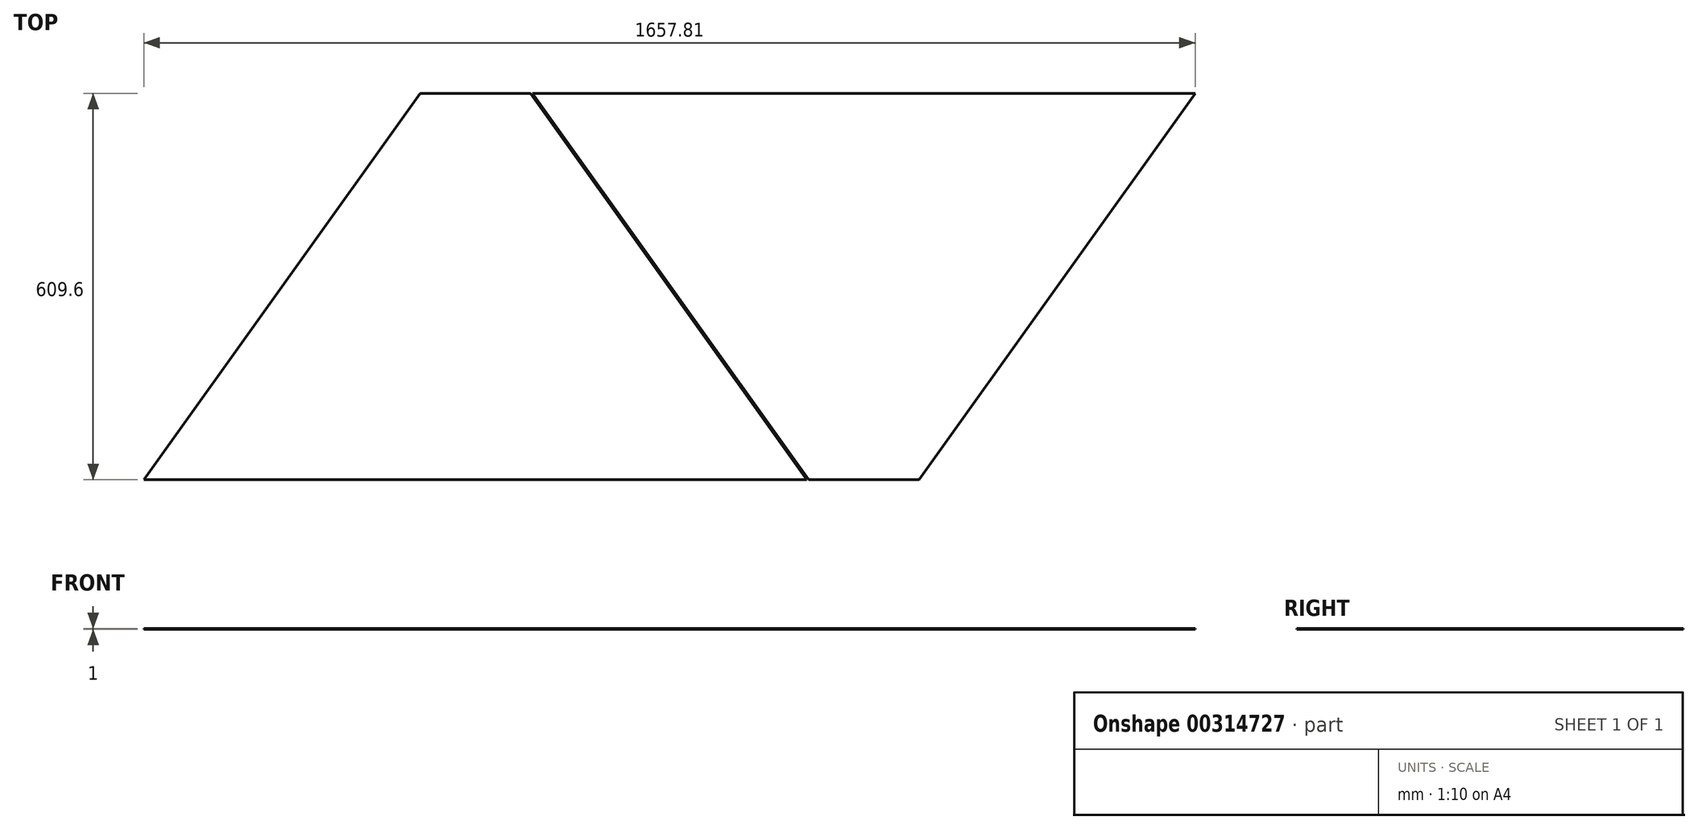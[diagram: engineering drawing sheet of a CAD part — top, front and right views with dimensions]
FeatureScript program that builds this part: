
annotation { "Feature Type Name" : "Feature", "Feature Type Description" : "" }
export const myFeature = defineFeature(function(context is Context, id is Id, definition is map)
    precondition{}
    {
        {
            var Q0;
            Q0=qCreatedBy(makeId("Top.planeOp"),FACE);
            var sketch = newSketch(context, id + "F0", { "sketchPlane" : qUnion([Q0])});
            skLineSegment(sketch, "E0", {"start": v(0, 0) * mm, "end": v(0, 609.6) * mm, "construction": true});
            skLineSegment(sketch, "E1", {"start": v(0, 0) * mm, "end": v(-522.6, 0) * mm});
            skLineSegment(sketch, "E2", {"start": v(0, 609.6) * mm, "end": v(-87, 609.6) * mm});
            skLineSegment(sketch, "E3", {"start": v(-87, 609.6) * mm, "end": v(-522.6, 0) * mm});
            skLineSegment(sketch, "E4.MirrorCS", {"start": v(0, 609.6) * mm, "end": v(87, 609.6) * mm});
            skLineSegment(sketch, "E5.MirrorCS", {"start": v(87, 609.6) * mm, "end": v(522.6, 0) * mm});
            skLineSegment(sketch, "E6.MirrorCS", {"start": v(0, 0) * mm, "end": v(522.6, 0) * mm});
            skLineSegment(sketch, "E7", {"start": v(525.6, 0) * mm, "end": v(612.6, 0) * mm});
            skLineSegment(sketch, "E8", {"start": v(525.6, 0) * mm, "end": v(90, 609.6) * mm});
            skLineSegment(sketch, "E9", {"start": v(612.6, 0) * mm, "end": v(699.6, 0) * mm});
            skLineSegment(sketch, "E10", {"start": v(90, 609.6) * mm, "end": v(612.6, 609.6) * mm});
            skLineSegment(sketch, "E11", {"start": v(612.6, 609.6) * mm, "end": v(1135.2, 609.6) * mm});
            skLineSegment(sketch, "E12", {"start": v(699.6, 0) * mm, "end": v(1135.2, 609.6) * mm});
            skSolve(sketch);
        }
        {
            var Q0;
            Q0=makeQuery(id+"F0.imprint","IMPRINT",FACE,{"disambiguationData":[TD([[makeQuery(id+"F0.imprint","IMPRINT",EDGE,{"derivedFrom":sQuery(id+"F0.wireOp",EDGE,"E1")}),-1.0]])]});
            extrude(context, id + "F1", {"entities" : qUnion([Q0]), "depth" : 1 * mm});
        }
        {
            var Q0;
            Q0=makeQuery(id+"F0.imprint","IMPRINT",FACE,{"disambiguationData":[TD([[makeQuery(id+"F0.imprint","IMPRINT",EDGE,{"derivedFrom":sQuery(id+"F0.wireOp",EDGE,"E7")}),1.0]])]});
            extrude(context, id + "F2", {"entities" : qUnion([Q0]), "depth" : 1 * mm});
        }
    });
